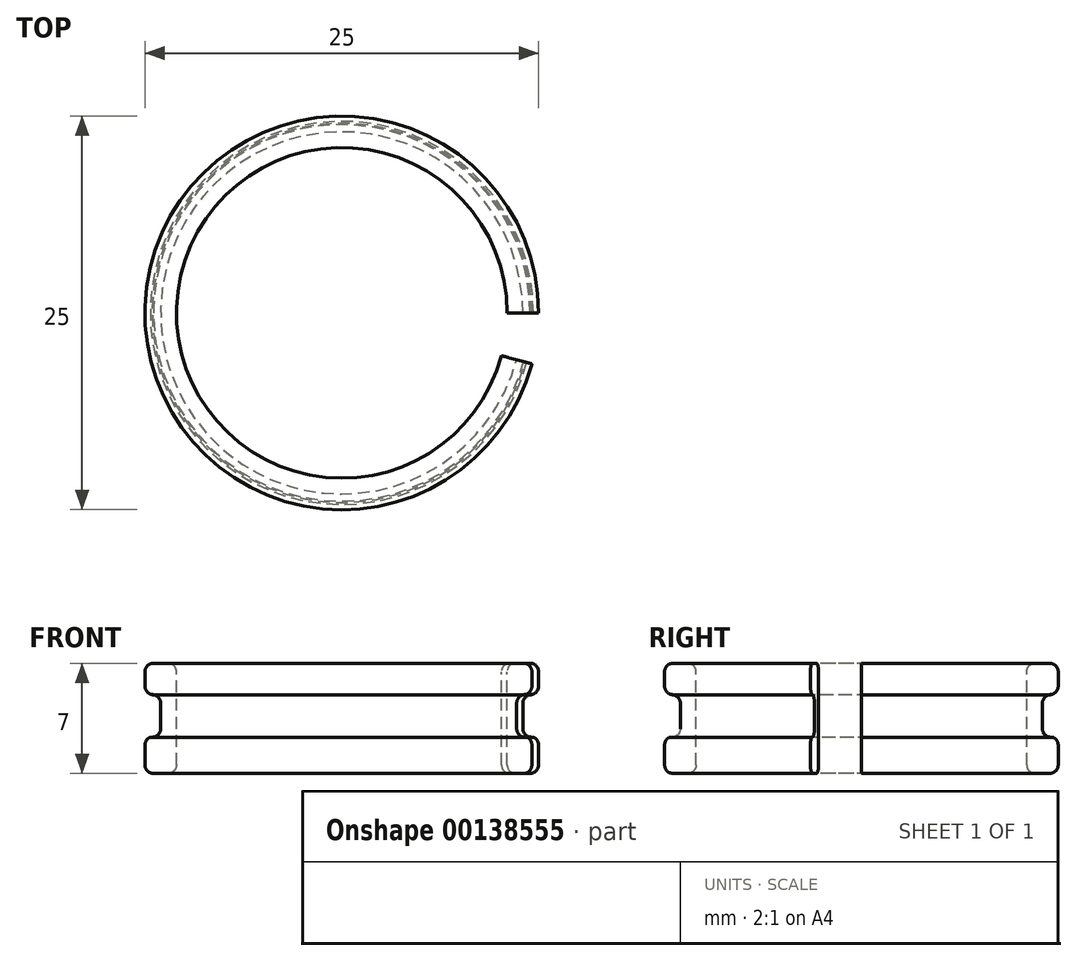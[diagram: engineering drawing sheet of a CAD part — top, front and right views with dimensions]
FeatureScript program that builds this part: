
annotation { "Feature Type Name" : "Feature", "Feature Type Description" : "" }
export const myFeature = defineFeature(function(context is Context, id is Id, definition is map)
    precondition{}
    {
        {
            var Q0;
            Q0=qCreatedBy(makeId("Front.planeOp"),FACE);
            var sketch = newSketch(context, id + "F0", { "sketchPlane" : qUnion([Q0])});
            skLineSegment(sketch, "E0", {"start": v(0, 58.33) * mm, "end": v(0, -74.17) * mm, "construction": true});
            skLineSegment(sketch, "E1", {"start": v(-11.04, 0) * mm, "end": v(-11.96, 0) * mm});
            skLineSegment(sketch, "E2", {"start": v(-12.5, 0.54) * mm, "end": v(-12.5, 1.8) * mm});
            skLineSegment(sketch, "E3", {"start": v(-11.5, 4.46) * mm, "end": v(-11.5, 13.04) * mm});
            skLineSegment(sketch, "E4", {"start": v(-11.96, 5) * mm, "end": v(-12.04, 5) * mm});
            skLineSegment(sketch, "E5", {"start": v(-12.5, 5.54) * mm, "end": v(-12.5, 6.46) * mm});
            skLineSegment(sketch, "E6", {"start": v(-11.96, 7) * mm, "end": v(-11.04, 7) * mm});
            skLineSegment(sketch, "E7", {"start": v(-10.5, 6.46) * mm, "end": v(-10.5, 0.54) * mm});
            skPoint(sketch, "E7.endSnap0", {"position": v(0.8, 0) * mm});
            skPoint(sketch, "E8.visualSharp", {"position": v(-11.5, 5) * mm});
            skArc(sketch, "E8.filletArc", {"start": v(-11.5, 4.46) * mm, "mid": v(-11.66, 4.84) * mm, "end": v(-12.04, 5) * mm});
            skPoint(sketch, "E9.visualSharp", {"position": v(-12.5, 5) * mm});
            skArc(sketch, "E9.filletArc", {"start": v(-12.5, 5.54) * mm, "mid": v(-12.34, 5.16) * mm, "end": v(-11.96, 5) * mm});
            skArc(sketch, "E10.filletArc", {"start": v(-12.17, 2.3) * mm, "mid": v(-12.4, 2.1) * mm, "end": v(-12.5, 1.8) * mm});
            skPoint(sketch, "E11.visualSharp", {"position": v(-12.5, 7) * mm});
            skArc(sketch, "E11.filletArc", {"start": v(-11.96, 7) * mm, "mid": v(-12.34, 6.84) * mm, "end": v(-12.5, 6.46) * mm});
            skPoint(sketch, "E12.visualSharp", {"position": v(-12.5, 0) * mm});
            skArc(sketch, "E12.filletArc", {"start": v(-12.5, 0.54) * mm, "mid": v(-12.34, 0.16) * mm, "end": v(-11.96, 0) * mm});
            skPoint(sketch, "E13.visualSharp", {"position": v(-10.5, 7) * mm});
            skArc(sketch, "E13.filletArc", {"start": v(-10.5, 6.46) * mm, "mid": v(-10.66, 6.84) * mm, "end": v(-11.04, 7) * mm});
            skPoint(sketch, "E14.newPointA", {"position": v(-10.5, 0) * mm});
            skPoint(sketch, "E14.newPointB", {"position": v(14.08, 0) * mm});
            skArc(sketch, "E14.filletArc", {"start": v(-11.04, 0) * mm, "mid": v(-10.66, 0.16) * mm, "end": v(-10.5, 0.54) * mm});
            skLineSegment(sketch, "E15", {"start": v(-11.5, 8.75) * mm, "end": v(0, 8.75) * mm, "construction": true});
            skLineSegment(sketch, "E16", {"start": v(-11.5, 13.04) * mm, "end": v(-11.5, 2.84) * mm});
            skLineSegment(sketch, "E17", {"start": v(-12.17, 2.3) * mm, "end": v(-12.04, 2.3) * mm});
            skPoint(sketch, "E18.visualSharp", {"position": v(-11.5, 2.3) * mm});
            skArc(sketch, "E18.filletArc", {"start": v(-12.04, 2.3) * mm, "mid": v(-11.66, 2.46) * mm, "end": v(-11.5, 2.84) * mm});
            skSolve(sketch);
        }
        {
            var Q0;
            Q0=makeQuery(id+"F0.imprint","IMPRINT",FACE,{"disambiguationData":[TD([[makeQuery(id+"F0.imprint","IMPRINT",EDGE,{"derivedFrom":sQuery(id+"F0.wireOp",EDGE,"E1")}),-1.0]])]});
            var Q1;
            Q1=makeQuery(id+"F0.imprint","IMPRINT",FACE,{"disambiguationData":[TD([[makeQuery(id+"F0.imprint","IMPRINT",EDGE,{"derivedFrom":sQuery(id+"F0.wireOp",EDGE,"E4")}),1.0]])]});
            var Q2;
            Q2=sQuery(id+"F0.wireOp",EDGE,"E0");
            revolve(context, id + "F1", {"entities" : qUnion([Q0, Q1]), "axis" : qUnion([Q2]), "revolveType" : RevolveType.FULL});
        }
        {
            var Q0;
            Q0=makeQuery(id+"F1.opRevolve","SWEPT_FACE",FACE,{"disambiguationData":[OSD([sQuery(id+"F0.wireOp",EDGE,"E6")])]});
            cPlane(context, id + "F2", {"entities" : qUnion([Q0]), "cplaneType" : CPlaneType.OFFSET, "offset" : 0 * mm, "width" : 150 * mm, "height" : 150 * mm});
        }
        {
            var Q0;
            Q0=qCreatedBy(id+"F2.planeOp",FACE);
            var sketch = newSketch(context, id + "F3", { "sketchPlane" : qUnion([Q0])});
            skLineSegment(sketch, "E19", {"start": v(0, 0) * mm, "end": v(12.5, 0) * mm});
            skLineSegment(sketch, "E20", {"start": v(0, 0) * mm, "end": v(12.07, -3.24) * mm});
            skCircle(sketch, "E21.0", {"center": v(0, 0) * mm, "radius": 10.5 * mm});
            skCircle(sketch, "E22.0", {"center": v(0, 0) * mm, "radius": 12.5 * mm});
            skSolve(sketch);
        }
        {
            var Q0;
            {var subQ0=sQuery(id+"F3.wireOp",EDGE,"E22.0");var subQ1=sQuery(id+"F3.wireOp",EDGE,"E19");var subQ2=makeQuery(id+"F3.imprint","INTERSECT",VERTEX,{"derivedFrom":[subQ1,subQ0]});Q0=makeQuery(id+"F3.imprint","IMPRINT",FACE,{"disambiguationData":[TD([[makeQuery(id+"F3.imprint","IMPRINT",EDGE,{"disambiguationData":[TD([[subQ2,1.0]])],"derivedFrom":subQ1}),-1.0]])]});}
            extrude(context, id + "F4", {"entities" : qUnion([Q0]), "operationType" : NewBodyOperationType.REMOVE, "endBound" : BoundingType.THROUGH_ALL, "oppositeDirection" : true, "depth" : 25 * mm});
        }
    });
